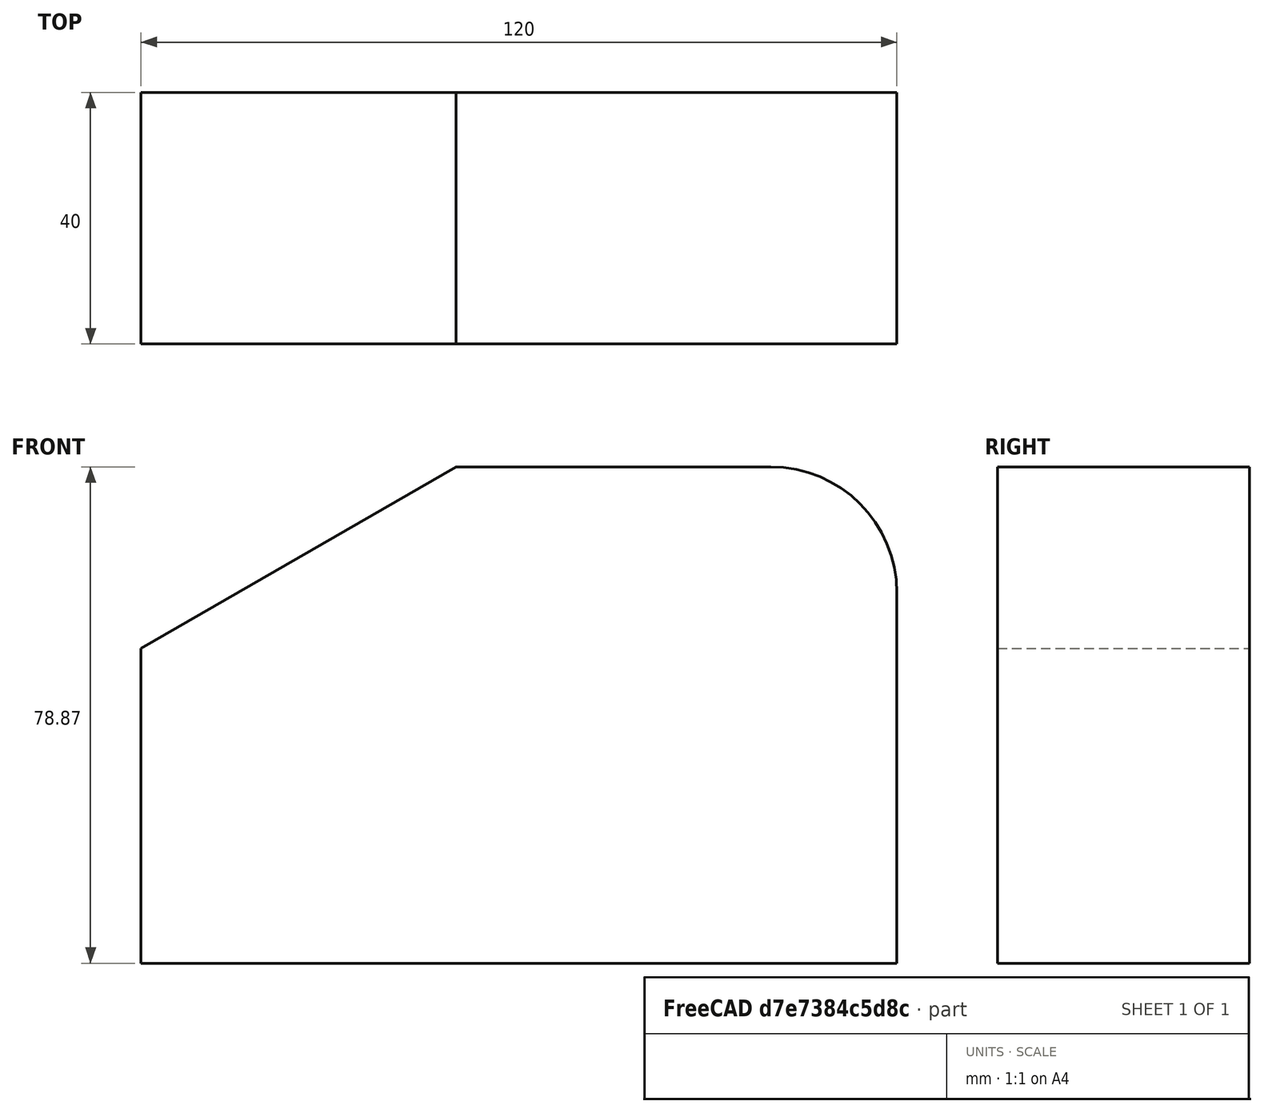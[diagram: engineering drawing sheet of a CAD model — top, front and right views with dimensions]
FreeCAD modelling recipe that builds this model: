
FCSTD DOCUMENT  (FreeCAD 0.17R13541 (Git))
Label: testFreeCad
License: All rights reserved
LicenseURL: http://en.wikipedia.org/wiki/All_rights_reserved
objects: Sketcher::SketchObject×2, PartDesign::Pad×1, PartDesign::Point×1, PartDesign::Plane×1, PartDesign::Body×1
note: 7 computed .brp shape members not serialized (recipe doc carries the construction recipe); baked Part::Feature solids carry a one-line shape summary decoded from their .brp

FEATURE [Sketcher::SketchObject] Sketch
  MapMode = 5
  Placement = pos=(0,0,0) rot=(1,0,0;1.5708rad)
  Support = -> [XZ_Plane]
  sketch-geometry (7):
    g0: LineSegment StartX=0 StartY=0 StartZ=0 EndX=120 EndY=0 EndZ=0
    g1: LineSegment StartX=120 StartY=0 StartZ=0 EndX=120 EndY=58.8675 EndZ=0
    g2: LineSegment StartX=0 StartY=0 StartZ=0 EndX=0 EndY=50 EndZ=0
    g3: LineSegment StartX=0 StartY=50 StartZ=0 EndX=50 EndY=78.8675 EndZ=0
    g4: LineSegment StartX=50 StartY=78.8675 StartZ=0 EndX=100 EndY=78.8675 EndZ=0
    g5: ArcOfCircle CenterX=100 CenterY=58.8675 CenterZ=0 NormalX=0 NormalY=0 NormalZ=1 AngleXU=0 Radius=20 StartAngle=0 EndAngle=1.5708
    g6: GeomPoint X=70.587 Y=39.0537 Z=0
  constraints (16):
    c: Coincident(g0,g-1)
    c: PointOnObject(g0,g-1)
    c: Coincident(g1,g0)
    c: Vertical(g1)
    c: Coincident(g2,g-1)
    c: PointOnObject(g2,g-2)
    c: Coincident(g3,g2)
    c: Coincident(g4,g3)
    c: Horizontal(g4)
    c: Angle(g0,g3) = 0.523599
    c: DistanceX(g0,g0) = 120
    c: DistanceY(g2,g2) = 50
    c: DistanceX(g3,g3) = 50
    c: Radius(g5) = 20
    c: Tangent(g5,g4) = 1.5708
    c: Tangent(g5,g1) = -1.5708
FEATURE [PartDesign::Pad] Pad
  Length = 40
  Length2 = 100
  Placement = pos=(0,0,0) rot=(1,0,0;1.5708rad)
  Profile = -> Sketch
  Reversed = true
  Type = 0
FEATURE [PartDesign::Point] DatumPoint
  AttacherType = Attacher::AttachEnginePoint
  MapMode = 37
  Placement = pos=(75,20,78.8675) rot=(0,0,1;0rad)
  Support = -> [Pad]
FEATURE [PartDesign::Plane] DatumPlane
  MapMode = 6
  Placement = pos=(75,20,78.8675) rot=(0,0,1;0rad)
  Support = -> [Pad,DatumPoint]
FEATURE [Sketcher::SketchObject] Sketch001
  MapMode = 5
  Placement = pos=(75,20,78.8675) rot=(0,0,1;0rad)
  Support = -> [DatumPlane]
  sketch-geometry (1):
    g0: Circle [constr] CenterX=0 CenterY=0 CenterZ=0 NormalX=0 NormalY=0 NormalZ=1 AngleXU=0 Radius=5
  constraints (2):
    c: Coincident(g0,g-1)
    c: Radius(g0) = 5
FEATURE [PartDesign::Body] Body  label="piece1"
  Group = -> [Sketch,Pad,DatumPoint,DatumPlane,Sketch001]
  Origin = -> Origin
  Tip = -> Pad
